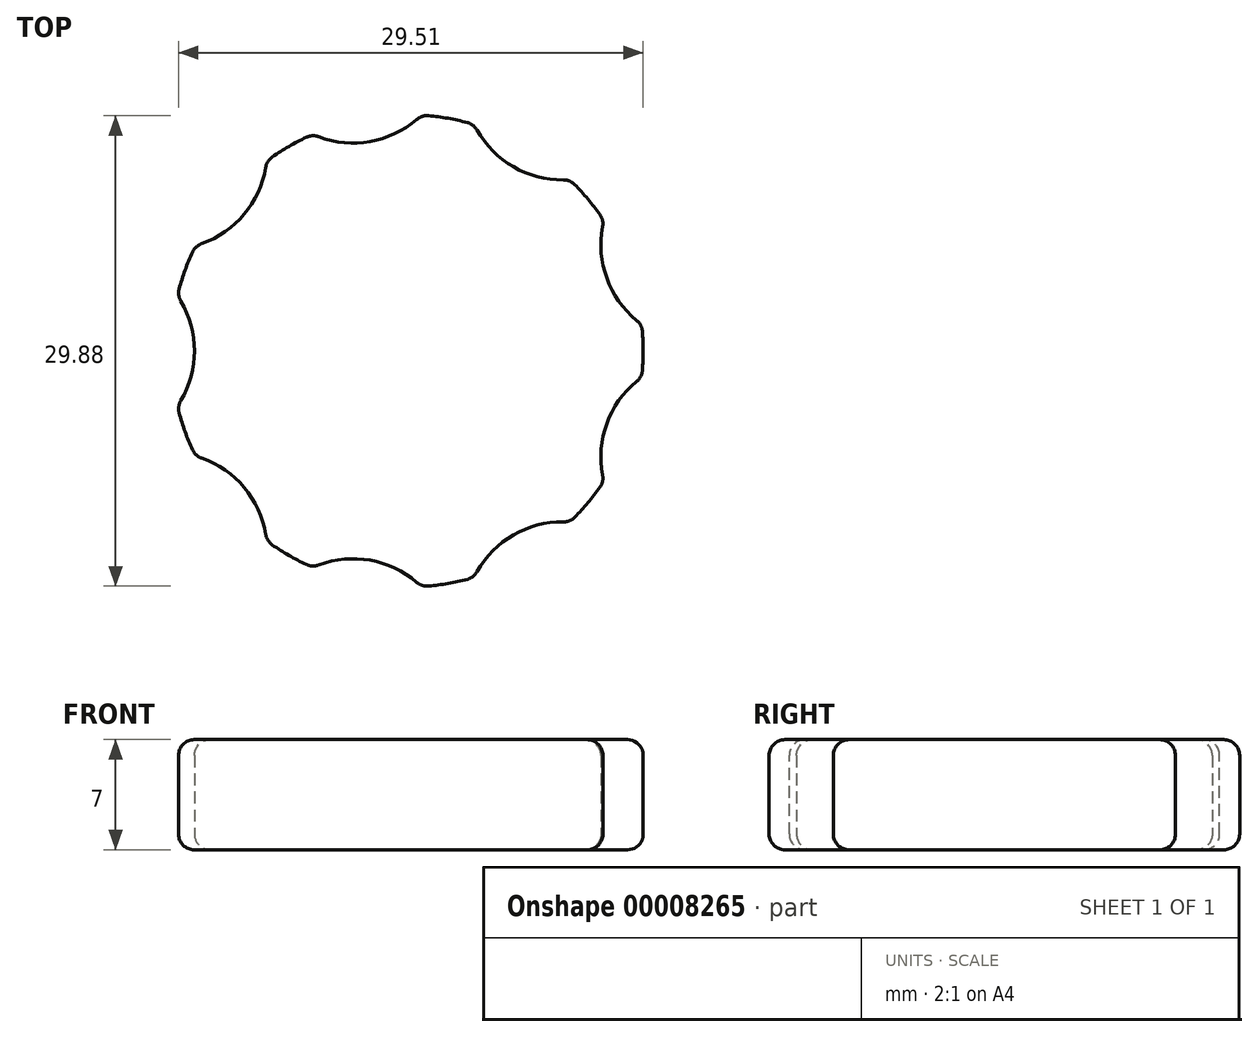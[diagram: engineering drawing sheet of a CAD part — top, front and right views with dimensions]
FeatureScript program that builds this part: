
annotation { "Feature Type Name" : "Feature", "Feature Type Description" : "" }
export const myFeature = defineFeature(function(context is Context, id is Id, definition is map)
    precondition{}
    {
        {
            var Q0;
            Q0=qCreatedBy(makeId("Top.planeOp"),FACE);
            var sketch = newSketch(context, id + "F0", { "sketchPlane" : qUnion([Q0])});
            skCircle(sketch, "E0", {"center": v(0, 0) * mm, "radius": 15 * mm});
            skArc(sketch, "E1", {"start": v(-14.59, -3.5) * mm, "mid": v(-13.5, 0) * mm, "end": v(-14.59, 3.5) * mm});
            skArc(sketch, "E2.1.0", {"start": v(-8.92, -12.06) * mm, "mid": v(-10.34, -8.68) * mm, "end": v(-13.42, -6.7) * mm});
            skArc(sketch, "E2.2.0", {"start": v(0.91, -14.97) * mm, "mid": v(-2.34, -13.3) * mm, "end": v(-5.98, -13.76) * mm});
            skArc(sketch, "E2.3.0", {"start": v(10.32, -10.88) * mm, "mid": v(6.75, -11.7) * mm, "end": v(4.26, -14.38) * mm});
            skArc(sketch, "E2.4.0", {"start": v(14.9, -1.7) * mm, "mid": v(12.69, -4.62) * mm, "end": v(12.5, -8.28) * mm});
            skArc(sketch, "E2.5.0", {"start": v(12.5, 8.28) * mm, "mid": v(12.69, 4.62) * mm, "end": v(14.9, 1.7) * mm});
            skArc(sketch, "E2.6.0", {"start": v(4.26, 14.38) * mm, "mid": v(6.75, 11.7) * mm, "end": v(10.32, 10.88) * mm});
            skArc(sketch, "E2.7.0", {"start": v(-5.98, 13.76) * mm, "mid": v(-2.34, 13.3) * mm, "end": v(0.91, 14.97) * mm});
            skArc(sketch, "E2.8.0", {"start": v(-13.42, 6.7) * mm, "mid": v(-10.34, 8.68) * mm, "end": v(-8.92, 12.06) * mm});
            skSolve(sketch);
        }
        {
            var Q0;
            Q0=makeQuery(id+"F0.imprint","IMPRINT",FACE,{"disambiguationData":[TD([[makeQuery(id+"F0.imprint","IMPRINT",EDGE,{"derivedFrom":sQuery(id+"F0.wireOp",EDGE,"E0")}),1.0]])]});
            extrude(context, id + "F1", {"entities" : qUnion([Q0]), "depth" : 7 * mm});
        }
        {
            var Q0;
            Q0=makeQuery(id+"F1.opExtrude","CAP_FACE",FACE,{"disambiguationData":[OSD([sQuery(id+"F0.wireOp",EDGE,"E0"),sQuery(id+"F0.wireOp",EDGE,"E1"),sQuery(id+"F0.wireOp",EDGE,"E2.1.0"),sQuery(id+"F0.wireOp",EDGE,"E2.2.0"),sQuery(id+"F0.wireOp",EDGE,"E2.3.0"),sQuery(id+"F0.wireOp",EDGE,"E2.4.0"),sQuery(id+"F0.wireOp",EDGE,"E2.5.0"),sQuery(id+"F0.wireOp",EDGE,"E2.6.0"),sQuery(id+"F0.wireOp",EDGE,"E2.7.0"),sQuery(id+"F0.wireOp",EDGE,"E2.8.0")])],"isStart":true});
            var Q1;
            Q1=makeQuery(id+"F1.opExtrude","CAP_FACE",FACE,{"disambiguationData":[OSD([sQuery(id+"F0.wireOp",EDGE,"E0"),sQuery(id+"F0.wireOp",EDGE,"E1"),sQuery(id+"F0.wireOp",EDGE,"E2.1.0"),sQuery(id+"F0.wireOp",EDGE,"E2.2.0"),sQuery(id+"F0.wireOp",EDGE,"E2.3.0"),sQuery(id+"F0.wireOp",EDGE,"E2.4.0"),sQuery(id+"F0.wireOp",EDGE,"E2.5.0"),sQuery(id+"F0.wireOp",EDGE,"E2.6.0"),sQuery(id+"F0.wireOp",EDGE,"E2.7.0"),sQuery(id+"F0.wireOp",EDGE,"E2.8.0")])],"isStart":false});
            var Q2;
            {var subQ0=sQuery(id+"F0.wireOp",EDGE,"E0");Q2=makeQuery(id+"F1.opExtrude","SWEPT_FACE",FACE,{"disambiguationData":[OSD([subQ0]),TDD([makeQuery(id+"F0.imprint","IMPRINT",EDGE,{"disambiguationData":[TD([[makeQuery(id+"F0.imprint","INTERSECT",VERTEX,{"disambiguationData":[OD(0.0)],"derivedFrom":[subQ0,sQuery(id+"F0.wireOp",EDGE,"E1")]}),-1.0]])],"derivedFrom":subQ0})])]});}
            var Q3;
            {var subQ0=sQuery(id+"F0.wireOp",EDGE,"E0");Q3=makeQuery(id+"F1.opExtrude","SWEPT_FACE",FACE,{"disambiguationData":[OSD([subQ0]),TDD([makeQuery(id+"F0.imprint","IMPRINT",EDGE,{"disambiguationData":[TD([[makeQuery(id+"F0.imprint","INTERSECT",VERTEX,{"disambiguationData":[OD(1.0)],"derivedFrom":[subQ0,sQuery(id+"F0.wireOp",EDGE,"E1")]}),1.0]])],"derivedFrom":subQ0})])]});}
            var Q4;
            {var subQ0=sQuery(id+"F0.wireOp",EDGE,"E0");Q4=makeQuery(id+"F1.opExtrude","SWEPT_FACE",FACE,{"disambiguationData":[OSD([subQ0]),TDD([makeQuery(id+"F0.imprint","IMPRINT",EDGE,{"disambiguationData":[TD([[makeQuery(id+"F0.imprint","INTERSECT",VERTEX,{"disambiguationData":[OD(0.0)],"derivedFrom":[subQ0,sQuery(id+"F0.wireOp",EDGE,"E2.7.0")]}),-1.0]])],"derivedFrom":subQ0})])]});}
            var Q5;
            {var subQ0=sQuery(id+"F0.wireOp",EDGE,"E0");Q5=makeQuery(id+"F1.opExtrude","SWEPT_FACE",FACE,{"disambiguationData":[OSD([subQ0]),TDD([makeQuery(id+"F0.imprint","IMPRINT",EDGE,{"disambiguationData":[TD([[makeQuery(id+"F0.imprint","INTERSECT",VERTEX,{"disambiguationData":[OD(0.0)],"derivedFrom":[subQ0,sQuery(id+"F0.wireOp",EDGE,"E2.6.0")]}),-1.0]])],"derivedFrom":subQ0})])]});}
            var Q6;
            {var subQ0=sQuery(id+"F0.wireOp",EDGE,"E0");Q6=makeQuery(id+"F1.opExtrude","SWEPT_FACE",FACE,{"disambiguationData":[OSD([subQ0]),TDD([makeQuery(id+"F0.imprint","IMPRINT",EDGE,{"disambiguationData":[TD([[makeQuery(id+"F0.imprint","INTERSECT",VERTEX,{"disambiguationData":[OD(0.0)],"derivedFrom":[subQ0,sQuery(id+"F0.wireOp",EDGE,"E2.5.0")]}),-1.0]])],"derivedFrom":subQ0})])]});}
            var Q7;
            {var subQ0=sQuery(id+"F0.wireOp",EDGE,"E0");Q7=makeQuery(id+"F1.opExtrude","SWEPT_FACE",FACE,{"disambiguationData":[OSD([subQ0]),TDD([makeQuery(id+"F0.imprint","IMPRINT",EDGE,{"disambiguationData":[TD([[makeQuery(id+"F0.imprint","INTERSECT",VERTEX,{"disambiguationData":[OD(0.0)],"derivedFrom":[subQ0,sQuery(id+"F0.wireOp",EDGE,"E2.4.0")]}),-1.0]])],"derivedFrom":subQ0})])]});}
            var Q8;
            {var subQ0=sQuery(id+"F0.wireOp",EDGE,"E0");Q8=makeQuery(id+"F1.opExtrude","SWEPT_FACE",FACE,{"disambiguationData":[OSD([subQ0]),TDD([makeQuery(id+"F0.imprint","IMPRINT",EDGE,{"disambiguationData":[TD([[makeQuery(id+"F0.imprint","INTERSECT",VERTEX,{"disambiguationData":[OD(0.0)],"derivedFrom":[subQ0,sQuery(id+"F0.wireOp",EDGE,"E2.3.0")]}),-1.0]])],"derivedFrom":subQ0})])]});}
            var Q9;
            {var subQ0=sQuery(id+"F0.wireOp",EDGE,"E0");Q9=makeQuery(id+"F1.opExtrude","SWEPT_FACE",FACE,{"disambiguationData":[OSD([subQ0]),TDD([makeQuery(id+"F0.imprint","IMPRINT",EDGE,{"disambiguationData":[TD([[makeQuery(id+"F0.imprint","INTERSECT",VERTEX,{"disambiguationData":[OD(0.0)],"derivedFrom":[subQ0,sQuery(id+"F0.wireOp",EDGE,"E2.2.0")]}),-1.0]])],"derivedFrom":subQ0})])]});}
            var Q10;
            {var subQ0=sQuery(id+"F0.wireOp",EDGE,"E0");Q10=makeQuery(id+"F1.opExtrude","SWEPT_FACE",FACE,{"disambiguationData":[OSD([subQ0]),TDD([makeQuery(id+"F0.imprint","IMPRINT",EDGE,{"disambiguationData":[TD([[makeQuery(id+"F0.imprint","INTERSECT",VERTEX,{"disambiguationData":[OD(0.0)],"derivedFrom":[subQ0,sQuery(id+"F0.wireOp",EDGE,"E2.1.0")]}),-1.0]])],"derivedFrom":subQ0})])]});}
            fillet(context, id + "F2", {"entities" : qUnion([Q0, Q1, Q2, Q3, Q4, Q5, Q6, Q7, Q8, Q9, Q10]), "radius" : 1 * mm, "tangentPropagation" : true, "allowEdgeOverflow" : false});
        }
    });
